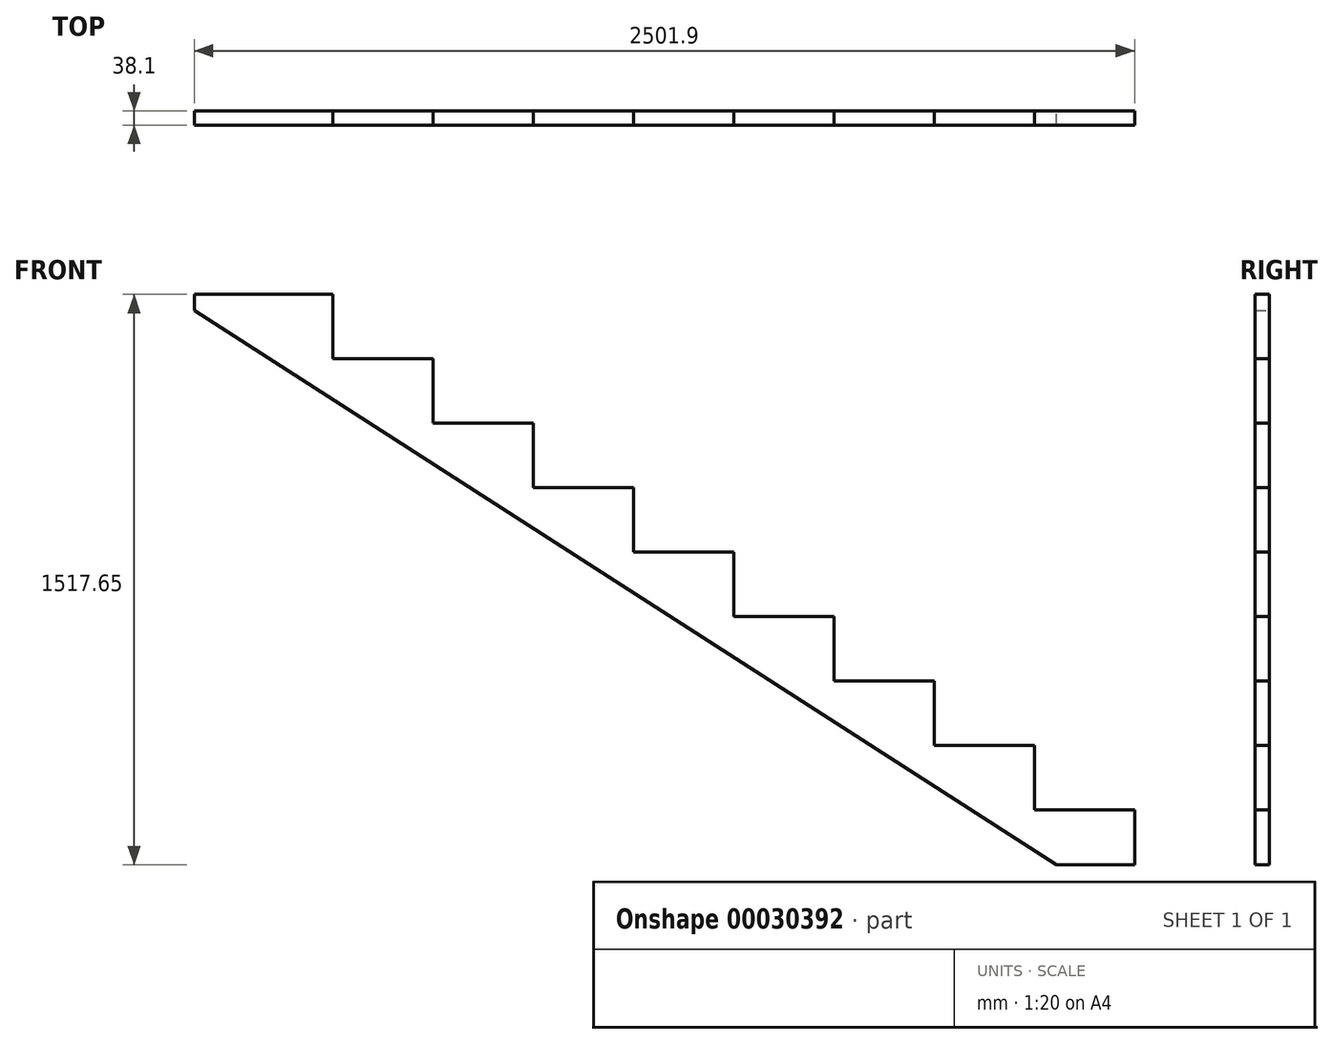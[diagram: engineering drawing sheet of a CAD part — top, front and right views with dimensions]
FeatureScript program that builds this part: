
annotation { "Feature Type Name" : "Feature", "Feature Type Description" : "" }
export const myFeature = defineFeature(function(context is Context, id is Id, definition is map)
    precondition{}
    {
        {
            var Q0;
            Q0=qCreatedBy(makeId("Front.planeOp"),FACE);
            var sketch = newSketch(context, id + "F0", { "sketchPlane" : qUnion([Q0])});
            skLineSegment(sketch, "E0", {"start": v(0, 0) * mm, "end": v(0, -42.55) * mm});
            skLineSegment(sketch, "E1", {"start": v(0, -42.55) * mm, "end": v(2294.6, -1517.65) * mm});
            skLineSegment(sketch, "E2", {"start": v(368.3, 0) * mm, "end": v(368.3, -171.45) * mm});
            skLineSegment(sketch, "E3", {"start": v(368.3, -171.45) * mm, "end": v(635, -171.45) * mm});
            skLineSegment(sketch, "E4", {"start": v(635, -171.45) * mm, "end": v(635, -342.9) * mm});
            skLineSegment(sketch, "E5", {"start": v(635, -342.9) * mm, "end": v(901.7, -342.9) * mm});
            skLineSegment(sketch, "E6", {"start": v(901.7, -342.9) * mm, "end": v(901.7, -514.35) * mm});
            skLineSegment(sketch, "E7", {"start": v(901.7, -514.35) * mm, "end": v(1168.4, -514.35) * mm});
            skLineSegment(sketch, "E8", {"start": v(1168.4, -514.35) * mm, "end": v(1168.4, -685.8) * mm});
            skLineSegment(sketch, "E9", {"start": v(1168.4, -685.8) * mm, "end": v(1435.1, -685.8) * mm});
            skLineSegment(sketch, "E10", {"start": v(1435.1, -685.8) * mm, "end": v(1435.1, -857.25) * mm});
            skLineSegment(sketch, "E11", {"start": v(1435.1, -857.25) * mm, "end": v(1701.8, -857.25) * mm});
            skLineSegment(sketch, "E12", {"start": v(1701.8, -857.25) * mm, "end": v(1701.8, -1028.7) * mm});
            skLineSegment(sketch, "E13", {"start": v(1701.8, -1028.7) * mm, "end": v(1968.5, -1028.7) * mm});
            skLineSegment(sketch, "E14", {"start": v(1968.5, -1028.7) * mm, "end": v(1968.5, -1200.15) * mm});
            skLineSegment(sketch, "E15", {"start": v(1968.5, -1200.15) * mm, "end": v(2235.2, -1200.15) * mm});
            skLineSegment(sketch, "E16", {"start": v(2235.2, -1200.15) * mm, "end": v(2235.2, -1371.6) * mm});
            skLineSegment(sketch, "E17", {"start": v(2235.2, -1371.6) * mm, "end": v(2501.9, -1371.6) * mm});
            skLineSegment(sketch, "E18", {"start": v(2501.9, -1517.65) * mm, "end": v(2294.6, -1517.65) * mm});
            skLineSegment(sketch, "E19", {"start": v(1168.4, -514.35) * mm, "end": v(1041.35, -711.98) * mm, "construction": true});
            skLineSegment(sketch, "E20", {"start": v(2501.9, -1371.6) * mm, "end": v(2501.9, -1517.65) * mm});
            skLineSegment(sketch, "E21", {"start": v(0, -42.55) * mm, "end": v(-122.63, 36.29) * mm, "construction": true});
            skLineSegment(sketch, "E22", {"start": v(-122.63, 36.29) * mm, "end": v(4.42, 233.92) * mm, "construction": true});
            skLineSegment(sketch, "E23", {"start": v(4.42, 233.92) * mm, "end": v(2568.33, -1414.3) * mm, "construction": true});
            skLineSegment(sketch, "E24", {"start": v(2568.33, -1414.3) * mm, "end": v(2441.28, -1611.94) * mm, "construction": true});
            skLineSegment(sketch, "E25", {"start": v(2441.28, -1611.94) * mm, "end": v(2294.6, -1517.65) * mm, "construction": true});
            skLineSegment(sketch, "E26", {"start": v(368.3, 0) * mm, "end": v(0, 0) * mm});
            skLineSegment(sketch, "E27", {"start": v(1701.8, -857.25) * mm, "end": v(1574.75, -1054.88) * mm, "construction": true});
            skSolve(sketch);
        }
        {
            var Q0;
            Q0 = qSketchRegion(id + "F0", true);
            extrude(context, id + "F1", {"entities" : qUnion([Q0]), "endBound" : BoundingType.SYMMETRIC, "depth" : 38.1 * mm});
        }
    });
